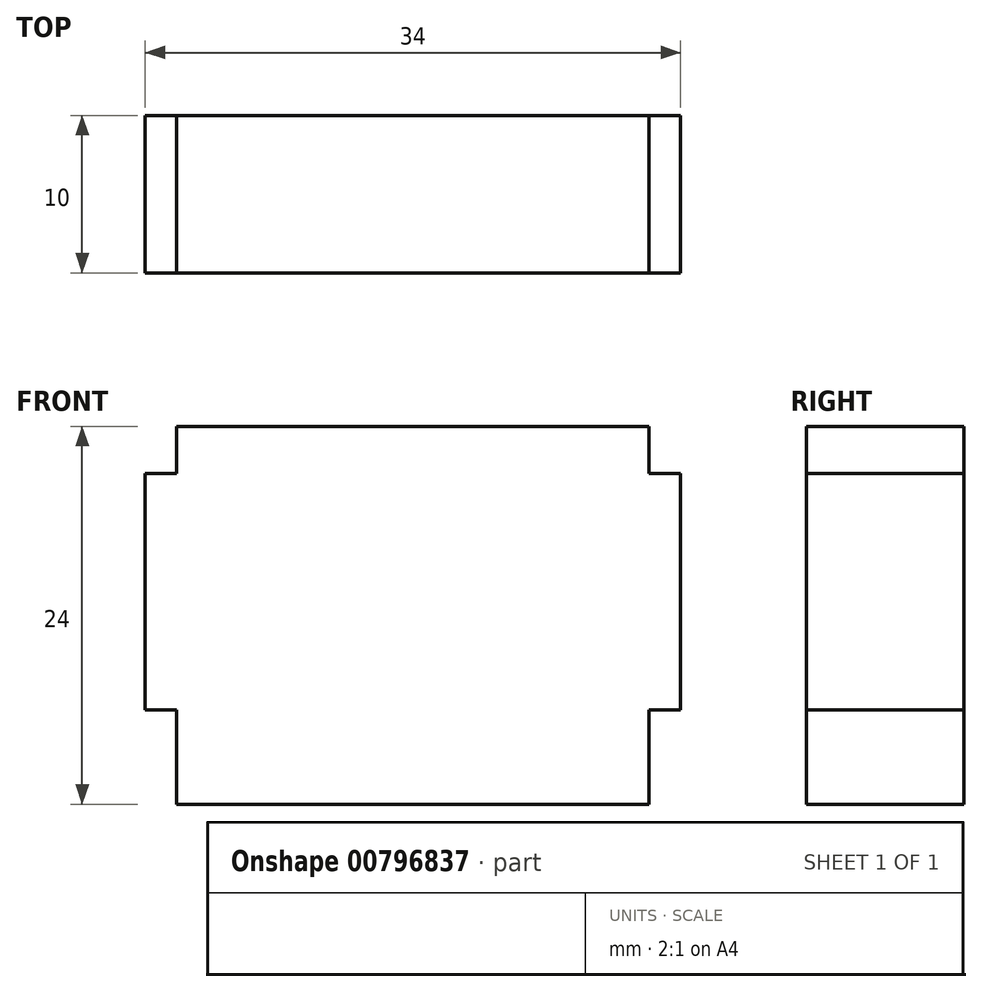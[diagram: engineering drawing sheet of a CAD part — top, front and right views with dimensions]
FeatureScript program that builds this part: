
annotation { "Feature Type Name" : "Feature", "Feature Type Description" : "" }
export const myFeature = defineFeature(function(context is Context, id is Id, definition is map)
    precondition{}
    {
        {
            var Q0;
            Q0=qCreatedBy(makeId("Top.planeOp"),FACE);
            var sketch = newSketch(context, id + "F0", { "sketchPlane" : qUnion([Q0])});
            skLineSegment(sketch, "E0.bottom", {"start": v(15, -5) * mm, "end": v(-15, -5) * mm});
            skLineSegment(sketch, "E0.top", {"start": v(15, 5) * mm, "end": v(-15, 5) * mm});
            skLineSegment(sketch, "E0.left", {"start": v(15, -5) * mm, "end": v(15, 5) * mm});
            skLineSegment(sketch, "E0.right", {"start": v(-15, -5) * mm, "end": v(-15, 5) * mm});
            skPoint(sketch, "E0.middle", {"position": v(0, 0) * mm});
            skSolve(sketch);
        }
        {
            var Q0;
            Q0=makeQuery(id+"F0.imprint","IMPRINT",FACE,{"disambiguationData":[TD([[makeQuery(id+"F0.imprint","IMPRINT",EDGE,{"derivedFrom":sQuery(id+"F0.wireOp",EDGE,"E0.bottom")}),-1.0]])]});
            extrude(context, id + "F1", {"entities" : qUnion([Q0]), "depth" : 6 * mm, "offsetDistance" : 25 * mm});
        }
        {
            var Q0;
            Q0=makeQuery(id+"F1.opExtrude","CAP_FACE",FACE,{"disambiguationData":[OSD([sQuery(id+"F0.wireOp",EDGE,"E0.bottom"),sQuery(id+"F0.wireOp",EDGE,"E0.top"),sQuery(id+"F0.wireOp",EDGE,"E0.left"),sQuery(id+"F0.wireOp",EDGE,"E0.right")])],"isStart":false});
            var sketch = newSketch(context, id + "F2", { "sketchPlane" : qUnion([Q0])});
            skLineSegment(sketch, "E1.bottom", {"start": v(17, -5) * mm, "end": v(-17, -5) * mm});
            skLineSegment(sketch, "E1.top", {"start": v(17, 5) * mm, "end": v(-17, 5) * mm});
            skLineSegment(sketch, "E1.left", {"start": v(17, -5) * mm, "end": v(17, 5) * mm});
            skLineSegment(sketch, "E1.right", {"start": v(-17, -5) * mm, "end": v(-17, 5) * mm});
            skPoint(sketch, "E1.middle", {"position": v(0, 0) * mm});
            skSolve(sketch);
        }
        {
            var Q0;
            Q0 = qSketchRegion(id + "F2", true);
            extrude(context, id + "F3", {"entities" : qUnion([Q0]), "operationType" : NewBodyOperationType.ADD, "depth" : 15 * mm, "offsetDistance" : 25 * mm});
        }
        {
            var Q0;
            Q0=makeQuery(id+"F3.opExtrude","CAP_FACE",FACE,{"disambiguationData":[OSD([sQuery(id+"F2.wireOp",EDGE,"E1.bottom"),sQuery(id+"F2.wireOp",EDGE,"E1.top"),sQuery(id+"F2.wireOp",EDGE,"E1.left"),sQuery(id+"F2.wireOp",EDGE,"E1.right")])],"isStart":false});
            var sketch = newSketch(context, id + "F4", { "sketchPlane" : qUnion([Q0])});
            skLineSegment(sketch, "E2.bottom", {"start": v(15, -5) * mm, "end": v(-15, -5) * mm});
            skLineSegment(sketch, "E2.top", {"start": v(15, 5) * mm, "end": v(-15, 5) * mm});
            skLineSegment(sketch, "E2.left", {"start": v(15, -5) * mm, "end": v(15, 5) * mm});
            skLineSegment(sketch, "E2.right", {"start": v(-15, -5) * mm, "end": v(-15, 5) * mm});
            skPoint(sketch, "E2.middle", {"position": v(0, 0) * mm});
            skSolve(sketch);
        }
        {
            var Q0;
            Q0 = qSketchRegion(id + "F4", true);
            extrude(context, id + "F5", {"entities" : qUnion([Q0]), "operationType" : NewBodyOperationType.ADD, "depth" : 3 * mm, "offsetDistance" : 25 * mm});
        }
    });
